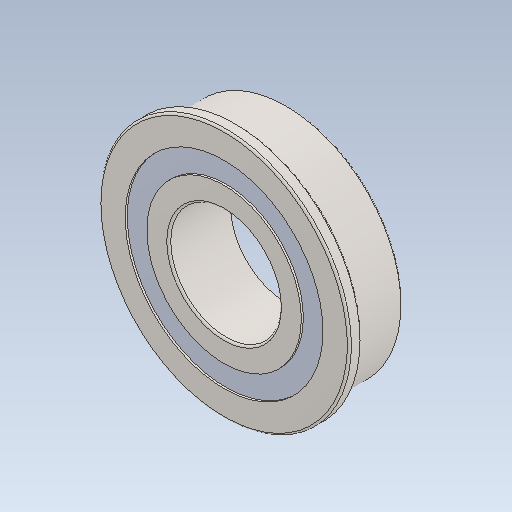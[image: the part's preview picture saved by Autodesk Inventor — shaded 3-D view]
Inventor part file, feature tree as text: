
AUTODESK INVENTOR PART (.ipt)
format: ipt  version: 2020 (Build 240168000, 168)  size: 192,512 bytes
history: native  units: in
note: dims shown in document units (in); Inventor stores cm internally (conversion verified against a paired STEP export)
features: fillet x1
ambient origin geometry x8: Origin, YZ Plane, XZ Plane, XY Plane, X Axis, Y Axis, Z Axis, Center Point
bodies: Solid1 (feature_tree)
feature tree (1):
  fillet  "Fillet1"  [1 undecoded]
note: 1 required parameter value undecoded (feature->parameter linkage not recoverable at this tier; creation-order binding heuristic only, values carry confidence <= 0.55)
